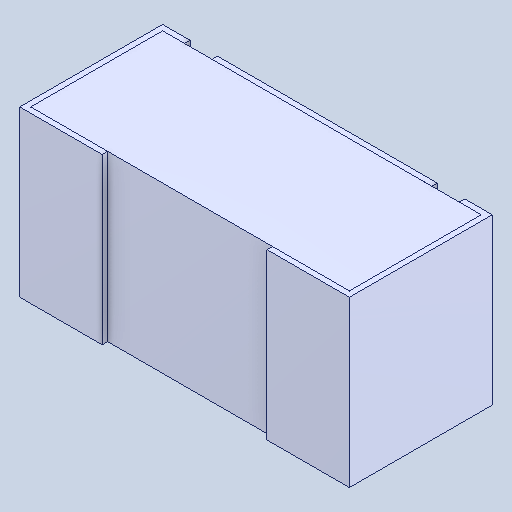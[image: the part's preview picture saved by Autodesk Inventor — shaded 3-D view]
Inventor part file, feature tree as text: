
AUTODESK INVENTOR PART (.ipt)
format: ipt  version: 2025 (Build 290162000, 162)  size: 110,080 bytes
history: native  units: mm
features: boolean_combine x2, other x1, mirror x1
ambient origin geometry x8: Origin, YZ Plane, XZ Plane, XY Plane, X Axis, Y Axis, Z Axis, Center Point
bodies: Solid1 (feature_tree), Solid2 (feature_tree), Solid3 (feature_tree), Solid4 (feature_tree)
feature tree (4):
  other  "Cut-Extrude1"
  boolean_combine  "Combine2"
  mirror  "Mirror1[3]"
  boolean_combine  "Combine1"
